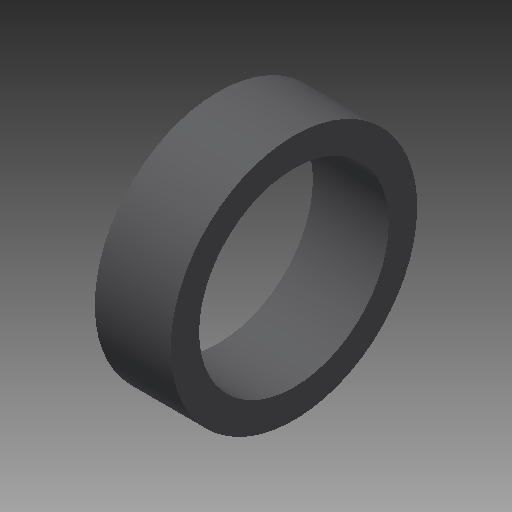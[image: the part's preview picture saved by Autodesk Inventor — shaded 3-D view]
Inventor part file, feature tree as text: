
AUTODESK INVENTOR PART (.ipt)
format: ipt  version: 2018 (Build 220112000, 112)  size: 104,960 bytes
history: native  units: mm
features: other x7, revolve x1, sketch x1
ambient origin geometry x8: Origin, YZ Plane, XZ Plane, XY Plane, X Axis, Y Axis, Z Axis, Center Point
bodies: Solid1 (feature_tree)
feature tree (9):
  revolve  "Revolution1"  [1 undecoded]
  other  "collar_XY"
  other  "collar_YZ"
  other  "collar_ZX"
  other  "collar_X"
  other  "collar_Y"
  other  "collar_Z"
  other  "collar_Center"
  sketch  "Sketch_1"  dims[d0=360.0deg d1=0.0mm]
note: 1 required parameter value undecoded (feature->parameter linkage not recoverable at this tier; creation-order binding heuristic only, values carry confidence <= 0.55)
